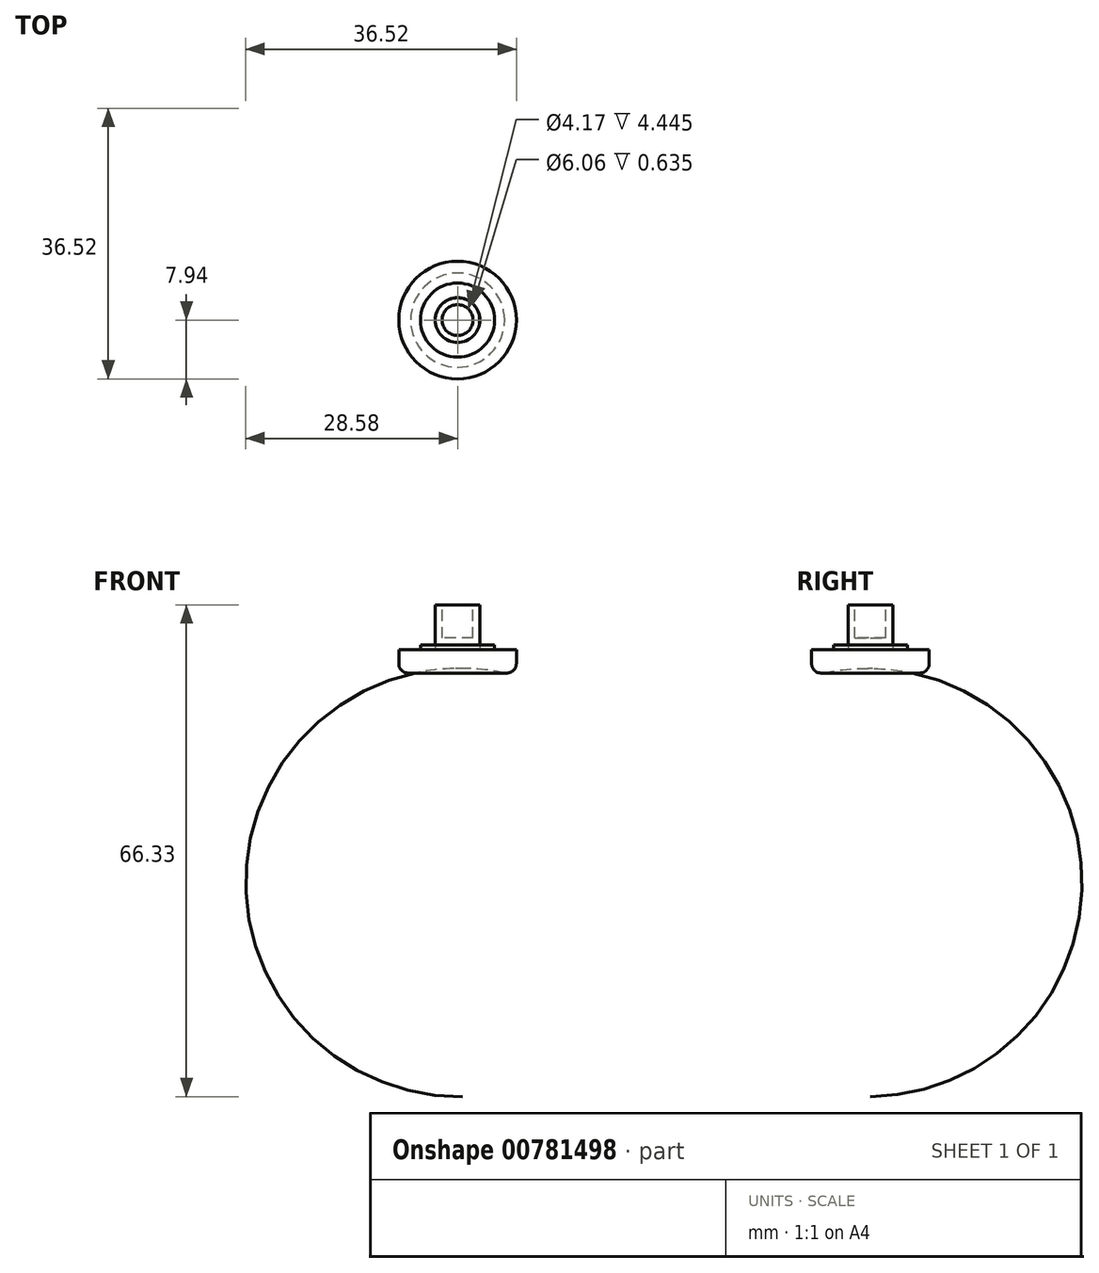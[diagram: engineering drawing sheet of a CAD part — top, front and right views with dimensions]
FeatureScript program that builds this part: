
annotation { "Feature Type Name" : "Feature", "Feature Type Description" : "" }
export const myFeature = defineFeature(function(context is Context, id is Id, definition is map)
    precondition{}
    {
        {
            var Q0;
            Q0=qCreatedBy(makeId("Top.planeOp"),FACE);
            var sketch = newSketch(context, id + "F0", { "sketchPlane" : qUnion([Q0])});
            skCircle(sketch, "E0", {"center": v(0, 0) * mm, "radius": 7.94 * mm});
            skSolve(sketch);
        }
        {
            var Q0;
            Q0=makeQuery(id+"F0.imprint","IMPRINT",FACE,{"disambiguationData":[TD([[makeQuery(id+"F0.imprint","IMPRINT",EDGE,{"derivedFrom":sQuery(id+"F0.wireOp",EDGE,"E0")}),1.0]])]});
            extrude(context, id + "F1", {"entities" : qUnion([Q0]), "depth" : 3.17 * mm, "offsetDistance" : 25.4 * mm});
        }
        {
            var Q0;
            Q0=makeQuery(id+"F1.opExtrude","CAP_FACE",FACE,{"disambiguationData":[OSD([sQuery(id+"F0.wireOp",EDGE,"E0")])],"isStart":false});
            var sketch = newSketch(context, id + "F2", { "sketchPlane" : qUnion([Q0])});
            skCircle(sketch, "E1", {"center": v(0, 0) * mm, "radius": 3 * mm});
            skSolve(sketch);
        }
        {
            var Q0;
            Q0 = qSketchRegion(id + "F2", true);
            extrude(context, id + "F3", {"entities" : qUnion([Q0]), "operationType" : NewBodyOperationType.ADD, "depth" : 6 * mm, "offsetDistance" : 25.4 * mm});
        }
        {
            var Q0;
            Q0=makeQuery(id+"F1.opExtrude","CAP_EDGE",EDGE,{"disambiguationData":[OSD([sQuery(id+"F0.wireOp",EDGE,"E0")])],"isStart":true});
            fillet(context, id + "F4", {"entities" : qUnion([Q0]), "radius" : 1.27 * mm, "tangentPropagation" : true, "allowEdgeOverflow" : false});
        }
        {
            var Q0;
            Q0=qCreatedBy(makeId("Front.planeOp"),FACE);
            var sketch = newSketch(context, id + "F5", { "sketchPlane" : qUnion([Q0])});
            skLineSegment(sketch, "E2", {"start": v(0, 0) * mm, "end": v(0, 0.64) * mm});
            skLineSegment(sketch, "E3", {"start": v(6.35, 0) * mm, "end": v(0, 0) * mm});
            skLineSegment(sketch, "E4", {"start": v(0, 0.64) * mm, "end": v(0.64, 0.64) * mm});
            skArc(sketch, "E5", {"start": v(6.35, 0) * mm, "mid": v(3.2, 0.5) * mm, "end": v(0, 0.64) * mm});
            skSolve(sketch);
        }
        {
            var Q0;
            Q0=qCreatedBy(makeId("Front.planeOp"),FACE);
            var sketch = newSketch(context, id + "F6", { "sketchPlane" : qUnion([Q0])});
            skLineSegment(sketch, "E6", {"start": v(0, 0) * mm, "end": v(0, 17.2) * mm, "construction": true});
            skSolve(sketch);
        }
        {
            var Q0;
            Q0 = qSketchRegion(id + "F5", true);
            var Q1;
            Q1=sQuery(id+"F6.wireOp",EDGE,"E6");
            revolve(context, id + "F7", {"operationType" : NewBodyOperationType.REMOVE, "surfaceOperationType" : NewSurfaceOperationType.NEW, "entities" : qUnion([Q0]), "axis" : qUnion([Q1]), "revolveType" : RevolveType.FULL, "oppositeDirection" : true});
        }
        {
            var Q0;
            Q0=makeQuery(id+"F3.opExtrude","CAP_FACE",FACE,{"disambiguationData":[OSD([sQuery(id+"F2.wireOp",EDGE,"E1")])],"isStart":false});
            var sketch = newSketch(context, id + "F8", { "sketchPlane" : qUnion([Q0])});
            skCircle(sketch, "E7", {"center": v(0, 0) * mm, "radius": 2.08 * mm});
            skSolve(sketch);
        }
        {
            var Q0;
            Q0 = qSketchRegion(id + "F8", true);
            extrude(context, id + "F9", {"entities" : qUnion([Q0]), "operationType" : NewBodyOperationType.REMOVE, "oppositeDirection" : true, "depth" : 4.44 * mm, "offsetDistance" : 25.4 * mm});
        }
        {
            var Q0;
            Q0=makeQuery(id+"F1.opExtrude","CAP_FACE",FACE,{"disambiguationData":[OSD([sQuery(id+"F0.wireOp",EDGE,"E0")])],"isStart":false});
            var sketch = newSketch(context, id + "F10", { "sketchPlane" : qUnion([Q0])});
            skCircle(sketch, "E8", {"center": v(0, 0) * mm, "radius": 5 * mm});
            skCircle(sketch, "E9", {"center": v(0, 0) * mm, "radius": 3.03 * mm});
            skSolve(sketch);
        }
        {
            var Q0;
            Q0=makeQuery(id+"F10.imprint","IMPRINT",FACE,{"disambiguationData":[TD([[makeQuery(id+"F10.imprint","IMPRINT",EDGE,{"derivedFrom":sQuery(id+"F10.wireOp",EDGE,"E8")}),1.0]])]});
            extrude(context, id + "F11", {"entities" : qUnion([Q0]), "operationType" : NewBodyOperationType.ADD, "depth" : 0.64 * mm, "offsetDistance" : 25.4 * mm});
        }
    });
